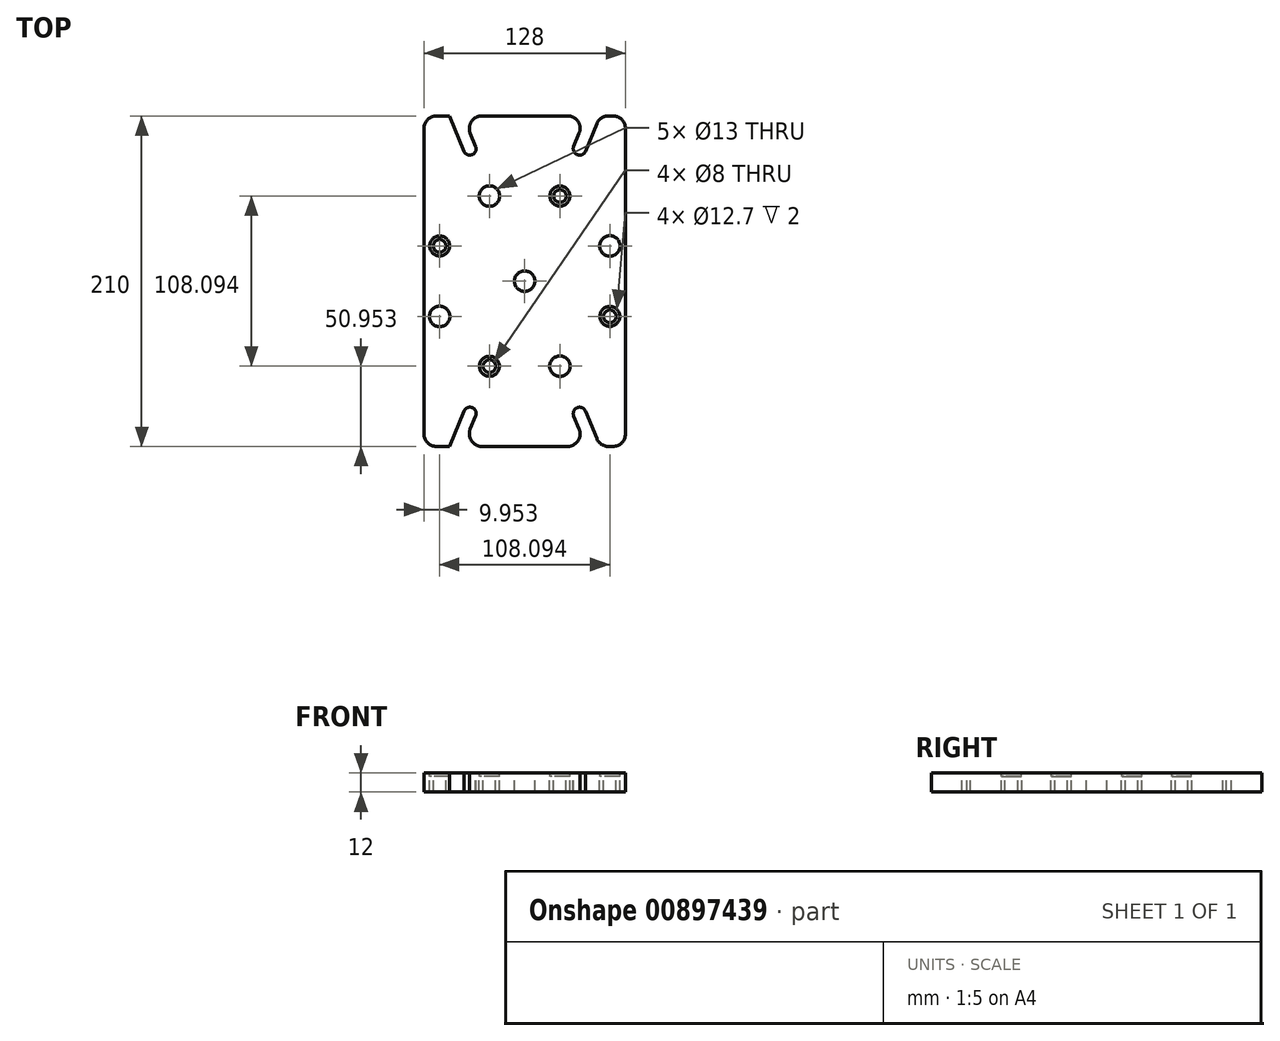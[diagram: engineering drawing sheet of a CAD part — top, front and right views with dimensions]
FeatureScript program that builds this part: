
annotation { "Feature Type Name" : "Feature", "Feature Type Description" : "" }
export const myFeature = defineFeature(function(context is Context, id is Id, definition is map)
    precondition{}
    {
        {
            var Q0;
            Q0=qCreatedBy(makeId("Top.planeOp"),FACE);
            var sketch = newSketch(context, id + "F0", { "sketchPlane" : qUnion([Q0])});
            skLineSegment(sketch, "E0.bottom", {"start": v(-64, 105) * mm, "end": v(64, 105) * mm});
            skLineSegment(sketch, "E0.top", {"start": v(-64, -105) * mm, "end": v(64, -105) * mm});
            skLineSegment(sketch, "E0.left", {"start": v(-64, 105) * mm, "end": v(-64, -105) * mm});
            skLineSegment(sketch, "E0.right", {"start": v(64, 105) * mm, "end": v(64, -105) * mm});
            skPoint(sketch, "E0.middle", {"position": v(0, 0) * mm});
            skSolve(sketch);
        }
        {
            var Q0;
            Q0=makeQuery(id+"F0.imprint","IMPRINT",FACE,{"disambiguationData":[TD([[makeQuery(id+"F0.imprint","IMPRINT",EDGE,{"derivedFrom":sQuery(id+"F0.wireOp",EDGE,"E0.bottom")}),-1.0]])]});
            extrude(context, id + "F1", {"entities" : qUnion([Q0]), "depth" : 12 * mm, "offsetDistance" : 25 * mm});
        }
        {
            var Q0;
            Q0=makeQuery(id+"F1.opExtrude","SWEPT_EDGE",EDGE,{"disambiguationData":[OSD([sQuery(id+"F0.wireOp",EDGE,"E0.top"),sQuery(id+"F0.wireOp",EDGE,"E0.left")])]});
            var Q1;
            Q1=makeQuery(id+"F1.opExtrude","SWEPT_EDGE",EDGE,{"disambiguationData":[OSD([sQuery(id+"F0.wireOp",EDGE,"E0.top"),sQuery(id+"F0.wireOp",EDGE,"E0.right")])]});
            var Q2;
            Q2=makeQuery(id+"F1.opExtrude","SWEPT_EDGE",EDGE,{"disambiguationData":[OSD([sQuery(id+"F0.wireOp",EDGE,"E0.bottom"),sQuery(id+"F0.wireOp",EDGE,"E0.right")])]});
            var Q3;
            Q3=makeQuery(id+"F1.opExtrude","SWEPT_EDGE",EDGE,{"disambiguationData":[OSD([sQuery(id+"F0.wireOp",EDGE,"E0.bottom"),sQuery(id+"F0.wireOp",EDGE,"E0.left")])]});
            fillet(context, id + "F2", {"entities" : qUnion([Q0, Q1, Q2, Q3]), "radius" : 8 * mm, "tangentPropagation" : true, "allowEdgeOverflow" : false});
        }
        {
            var Q0;
            Q0=makeQuery(id+"F1.opExtrude","CAP_FACE",FACE,{"disambiguationData":[OSD([sQuery(id+"F0.wireOp",EDGE,"E0.bottom"),sQuery(id+"F0.wireOp",EDGE,"E0.top"),sQuery(id+"F0.wireOp",EDGE,"E0.left"),sQuery(id+"F0.wireOp",EDGE,"E0.right")])],"isStart":false});
            var sketch = newSketch(context, id + "F3", { "sketchPlane" : qUnion([Q0])});
            skCircle(sketch, "E1", {"center": v(0, 0) * mm, "radius": 58.5 * mm, "construction": true});
            skLineSegment(sketch, "E2", {"start": v(77.06, 0) * mm, "end": v(-72.15, 0) * mm, "construction": true});
            skLineSegment(sketch, "E3", {"start": v(0, -115.81) * mm, "end": v(0, 119.74) * mm, "construction": true});
            skPoint(sketch, "E3.endSnap0", {"position": v(0, 105) * mm});
            skLineSegment(sketch, "E4", {"start": v(0, 0) * mm, "end": v(-83.82, 34.72) * mm, "construction": true});
            skCircle(sketch, "E5", {"center": v(-54.05, 22.39) * mm, "radius": 6.35 * mm});
            skCircle(sketch, "E6", {"center": v(-54.05, 22.39) * mm, "radius": 4 * mm});
            skLineSegment(sketch, "E7", {"start": v(0, 0) * mm, "end": v(59.7, -24.73) * mm, "construction": true});
            skLineSegment(sketch, "E8", {"start": v(0, 0) * mm, "end": v(59.72, 24.74) * mm, "construction": true});
            skLineSegment(sketch, "E9", {"start": v(47.91, -47.91) * mm, "end": v(0, 0) * mm, "construction": true});
            skLineSegment(sketch, "E10", {"start": v(0, 0) * mm, "end": v(-47.85, -47.85) * mm, "construction": true});
            skLineSegment(sketch, "E11", {"start": v(-47.85, -47.85) * mm, "end": v(0, 0) * mm, "construction": true});
            skLineSegment(sketch, "E12", {"start": v(0, 0) * mm, "end": v(-49.76, 49.76) * mm, "construction": true});
            skLineSegment(sketch, "E13", {"start": v(0, 0) * mm, "end": v(48.36, 48.36) * mm, "construction": true});
            skLineSegment(sketch, "E14", {"start": v(0, 0) * mm, "end": v(52.16, -125.92) * mm, "construction": true});
            skLineSegment(sketch, "E15", {"start": v(0, 0) * mm, "end": v(-48.89, -118.03) * mm, "construction": true});
            skLineSegment(sketch, "E16", {"start": v(0, 0) * mm, "end": v(-60.76, -25.17) * mm, "construction": true});
            skLineSegment(sketch, "E17", {"start": v(0, 0) * mm, "end": v(-48.6, 117.35) * mm, "construction": true});
            skLineSegment(sketch, "E18", {"start": v(0, 0) * mm, "end": v(49.9, 120.5) * mm, "construction": true});
            skCircle(sketch, "E19", {"center": v(54.05, -22.39) * mm, "radius": 4 * mm});
            skCircle(sketch, "E20", {"center": v(54.05, -22.39) * mm, "radius": 6.35 * mm});
            skCircle(sketch, "E21", {"center": v(-22.39, -54.05) * mm, "radius": 6.35 * mm});
            skCircle(sketch, "E22", {"center": v(-22.39, -54.05) * mm, "radius": 4 * mm});
            skCircle(sketch, "E23", {"center": v(22.39, 54.05) * mm, "radius": 6.35 * mm});
            skCircle(sketch, "E24", {"center": v(22.39, 54.05) * mm, "radius": 4 * mm});
            skCircle(sketch, "E25", {"center": v(-22.39, 54.05) * mm, "radius": 6.5 * mm});
            skCircle(sketch, "E26", {"center": v(-54.05, -22.39) * mm, "radius": 6.5 * mm});
            skCircle(sketch, "E27", {"center": v(22.39, -54.05) * mm, "radius": 6.5 * mm});
            skCircle(sketch, "E28", {"center": v(54.05, 22.39) * mm, "radius": 6.5 * mm});
            skSolve(sketch);
        }
        {
            var Q0;
            Q0=makeQuery(id+"F3.imprint","IMPRINT",FACE,{"disambiguationData":[TD([[makeQuery(id+"F3.imprint","IMPRINT",EDGE,{"derivedFrom":sQuery(id+"F3.wireOp",EDGE,"E25")}),1.0]])]});
            var Q1;
            Q1=makeQuery(id+"F3.imprint","IMPRINT",FACE,{"disambiguationData":[TD([[makeQuery(id+"F3.imprint","IMPRINT",EDGE,{"derivedFrom":sQuery(id+"F3.wireOp",EDGE,"E6")}),1.0]])]});
            var Q2;
            Q2=makeQuery(id+"F3.imprint","IMPRINT",FACE,{"disambiguationData":[TD([[makeQuery(id+"F3.imprint","IMPRINT",EDGE,{"derivedFrom":sQuery(id+"F3.wireOp",EDGE,"E26")}),1.0]])]});
            var Q3;
            Q3=makeQuery(id+"F3.imprint","IMPRINT",FACE,{"disambiguationData":[TD([[makeQuery(id+"F3.imprint","IMPRINT",EDGE,{"derivedFrom":sQuery(id+"F3.wireOp",EDGE,"E22")}),1.0]])]});
            var Q4;
            Q4=makeQuery(id+"F3.imprint","IMPRINT",FACE,{"disambiguationData":[TD([[makeQuery(id+"F3.imprint","IMPRINT",EDGE,{"derivedFrom":sQuery(id+"F3.wireOp",EDGE,"E27")}),1.0]])]});
            var Q5;
            Q5=makeQuery(id+"F3.imprint","IMPRINT",FACE,{"disambiguationData":[TD([[makeQuery(id+"F3.imprint","IMPRINT",EDGE,{"derivedFrom":sQuery(id+"F3.wireOp",EDGE,"E19")}),1.0]])]});
            var Q6;
            Q6=makeQuery(id+"F3.imprint","IMPRINT",FACE,{"disambiguationData":[TD([[makeQuery(id+"F3.imprint","IMPRINT",EDGE,{"derivedFrom":sQuery(id+"F3.wireOp",EDGE,"E28")}),1.0]])]});
            var Q7;
            Q7=makeQuery(id+"F3.imprint","IMPRINT",FACE,{"disambiguationData":[TD([[makeQuery(id+"F3.imprint","IMPRINT",EDGE,{"derivedFrom":sQuery(id+"F3.wireOp",EDGE,"E24")}),1.0]])]});
            extrude(context, id + "F4", {"entities" : qUnion([Q0, Q1, Q2, Q3, Q4, Q5, Q6, Q7]), "operationType" : NewBodyOperationType.REMOVE, "oppositeDirection" : true, "depth" : 25 * mm, "offsetDistance" : 25 * mm});
        }
        {
            var Q0;
            Q0=makeQuery(id+"F3.imprint","IMPRINT",FACE,{"disambiguationData":[TD([[makeQuery(id+"F3.imprint","IMPRINT",EDGE,{"derivedFrom":sQuery(id+"F3.wireOp",EDGE,"E5")}),1.0]])]});
            var Q1;
            Q1=makeQuery(id+"F3.imprint","IMPRINT",FACE,{"disambiguationData":[TD([[makeQuery(id+"F3.imprint","IMPRINT",EDGE,{"derivedFrom":sQuery(id+"F3.wireOp",EDGE,"E21")}),1.0]])]});
            var Q2;
            Q2=makeQuery(id+"F3.imprint","IMPRINT",FACE,{"disambiguationData":[TD([[makeQuery(id+"F3.imprint","IMPRINT",EDGE,{"derivedFrom":sQuery(id+"F3.wireOp",EDGE,"E19")}),-1.0]])]});
            var Q3;
            Q3=makeQuery(id+"F3.imprint","IMPRINT",FACE,{"disambiguationData":[TD([[makeQuery(id+"F3.imprint","IMPRINT",EDGE,{"derivedFrom":sQuery(id+"F3.wireOp",EDGE,"E23")}),1.0]])]});
            extrude(context, id + "F5", {"entities" : qUnion([Q0, Q1, Q2, Q3]), "operationType" : NewBodyOperationType.REMOVE, "oppositeDirection" : true, "depth" : 2 * mm, "offsetDistance" : 25 * mm});
        }
        {
            var Q0;
            Q0=makeQuery(id+"F3.imprint","IMPRINT",FACE,{"disambiguationData":[TD([[makeQuery(id+"F3.imprint","IMPRINT",EDGE,{"derivedFrom":sQuery(id+"F3.wireOp",EDGE,"E5")}),-1.0]])]});
            var sketch = newSketch(context, id + "F6", { "sketchPlane" : qUnion([Q0])});
            skCircle(sketch, "E29", {"center": v(0, 0) * mm, "radius": 91 * mm, "construction": true});
            skLineSegment(sketch, "E30", {"start": v(0, 0) * mm, "end": v(-54.7, 132.08) * mm, "construction": true});
            skLineSegment(sketch, "E31", {"start": v(0, 0) * mm, "end": v(-105.92, 0) * mm, "construction": true});
            skLineSegment(sketch, "E32", {"start": v(0, 0) * mm, "end": v(-51.64, -124.67) * mm, "construction": true});
            skLineSegment(sketch, "E33", {"start": v(0, 0) * mm, "end": v(47.52, -114.72) * mm, "construction": true});
            skLineSegment(sketch, "E34", {"start": v(0, 0) * mm, "end": v(51.4, 124.11) * mm, "construction": true});
            skArc(sketch, "E35", {"start": v(-38.55, 82.62) * mm, "mid": v(-33.3, 80.38) * mm, "end": v(-31.16, 85.68) * mm});
            skArc(sketch, "E36", {"start": v(31.16, 85.68) * mm, "mid": v(33.3, 80.38) * mm, "end": v(38.55, 82.62) * mm});
            skLineSegment(sketch, "E37", {"start": v(-38.49, 82.46) * mm, "end": v(-48.1, 105.67) * mm});
            skLineSegment(sketch, "E38", {"start": v(-31.1, 85.52) * mm, "end": v(-39.44, 105.67) * mm});
            skLineSegment(sketch, "E39", {"start": v(-48.1, 105.67) * mm, "end": v(-39.44, 105.67) * mm});
            skPoint(sketch, "E40.orphan", {"position": v(-39.16, 104.99) * mm});
            skPoint(sketch, "E41.orphan", {"position": v(-39.16, 105.67) * mm});
            skLineSegment(sketch, "E42.MirrorCS", {"start": v(38.49, 82.46) * mm, "end": v(48.1, 105.67) * mm});
            skArc(sketch, "E43.MirrorCS", {"start": v(38.55, 82.62) * mm, "mid": v(33.3, 80.38) * mm, "end": v(31.16, 85.68) * mm});
            skArc(sketch, "E44.MirrorCS", {"start": v(38.55, 82.62) * mm, "mid": v(38.52, 82.54) * mm, "end": v(38.49, 82.46) * mm});
            skLineSegment(sketch, "E45.MirrorCS", {"start": v(31.1, 85.52) * mm, "end": v(39.44, 105.67) * mm});
            skLineSegment(sketch, "E46.MirrorCS", {"start": v(48.1, 105.67) * mm, "end": v(39.44, 105.67) * mm});
            skLineSegment(sketch, "E47.MirrorCS", {"start": v(-38.49, -82.46) * mm, "end": v(-48.1, -105.67) * mm});
            skArc(sketch, "E48.MirrorCS", {"start": v(-38.55, -82.62) * mm, "mid": v(-33.3, -80.38) * mm, "end": v(-31.16, -85.68) * mm});
            skLineSegment(sketch, "E49.MirrorCS", {"start": v(-31.1, -85.52) * mm, "end": v(-39.44, -105.67) * mm});
            skLineSegment(sketch, "E50.MirrorCS", {"start": v(-48.1, -105.67) * mm, "end": v(-39.44, -105.67) * mm});
            skLineSegment(sketch, "E51.MirrorCS", {"start": v(38.49, -82.46) * mm, "end": v(48.1, -105.67) * mm});
            skArc(sketch, "E52.MirrorCS", {"start": v(38.55, -82.62) * mm, "mid": v(33.3, -80.38) * mm, "end": v(31.16, -85.68) * mm});
            skLineSegment(sketch, "E53.MirrorCS", {"start": v(31.1, -85.52) * mm, "end": v(39.44, -105.67) * mm});
            skLineSegment(sketch, "E54.MirrorCS", {"start": v(48.1, -105.67) * mm, "end": v(39.44, -105.67) * mm});
            skArc(sketch, "E55.trimOffspring", {"start": v(31.1, 85.52) * mm, "mid": v(31.13, 85.6) * mm, "end": v(31.16, 85.68) * mm});
            skSolve(sketch);
        }
        {
            var Q0;
            {var subQ0=sQuery(id+"F6.wireOp",EDGE,"E38");var subQ1=sQuery(id+"F6.wireOp",EDGE,"E35");var subQ9=makeQuery(id+"F6.imprint","INTERSECT",VERTEX,{"disambiguationData":[OD(0.0)],"derivedFrom":[subQ1,subQ0]});Q0=makeQuery(id+"F6.imprint","IMPRINT",FACE,{"disambiguationData":[TD([[makeQuery(id+"F6.imprint","IMPRINT",EDGE,{"disambiguationData":[TD([[subQ9,1.0]])],"derivedFrom":subQ1}),1.0]])]});}
            var Q1;
            {var subQ1=sQuery(id+"F6.wireOp",EDGE,"E48.MirrorCS");var subQ5=sQuery(id+"F6.wireOp",EDGE,"E47.MirrorCS");var subQ6=makeQuery(id+"F6.imprint","INTERSECT",VERTEX,{"disambiguationData":[OD(0.0)],"derivedFrom":[subQ5,subQ1]});Q1=makeQuery(id+"F6.imprint","IMPRINT",FACE,{"disambiguationData":[TD([[makeQuery(id+"F6.imprint","IMPRINT",EDGE,{"disambiguationData":[TD([[subQ6,-1.0]])],"derivedFrom":subQ5}),1.0]])]});}
            var Q2;
            {var subQ0=sQuery(id+"F6.wireOp",EDGE,"E52.MirrorCS");var subQ1=sQuery(id+"F6.wireOp",EDGE,"E51.MirrorCS");var subQ8=makeQuery(id+"F6.imprint","INTERSECT",VERTEX,{"disambiguationData":[OD(0.0)],"derivedFrom":[subQ1,subQ0]});Q2=makeQuery(id+"F6.imprint","IMPRINT",FACE,{"disambiguationData":[TD([[makeQuery(id+"F6.imprint","IMPRINT",EDGE,{"disambiguationData":[TD([[subQ8,-1.0]])],"derivedFrom":subQ1}),-1.0]])]});}
            var Q3;
            {var subQ0=sQuery(id+"F6.wireOp",EDGE,"E45.MirrorCS");var subQ1=sQuery(id+"F6.wireOp",EDGE,"E36");var subQ9=makeQuery(id+"F6.imprint","INTERSECT",VERTEX,{"disambiguationData":[OD(1.0)],"derivedFrom":[subQ1,subQ0]});Q3=makeQuery(id+"F6.imprint","IMPRINT",FACE,{"disambiguationData":[TD([[makeQuery(id+"F6.imprint","IMPRINT",EDGE,{"disambiguationData":[TD([[subQ9,-1.0]])],"derivedFrom":subQ1}),1.0]])]});}
            extrude(context, id + "F7", {"entities" : qUnion([Q0, Q1, Q2, Q3]), "operationType" : NewBodyOperationType.REMOVE, "oppositeDirection" : true, "depth" : 25 * mm, "offsetDistance" : 25 * mm});
        }
        {
            var Q0;
            Q0=makeQuery(id+"F7.boolean.opBoolean","COPY",EDGE,{"derivedFrom":makeQuery(id+"F7.opExtrude","SWEPT_EDGE",EDGE,{"disambiguationData":[OSD([sQuery(id+"F0.wireOp",EDGE,"E0.bottom"),sQuery(id+"F6.wireOp",EDGE,"E37")])]})});
            var Q1;
            Q1=makeQuery(id+"F7.boolean.opBoolean","COPY",EDGE,{"derivedFrom":makeQuery(id+"F7.opExtrude","SWEPT_EDGE",EDGE,{"disambiguationData":[OSD([sQuery(id+"F0.wireOp",EDGE,"E0.bottom"),sQuery(id+"F6.wireOp",EDGE,"E38")])]})});
            var Q2;
            Q2=makeQuery(id+"F7.boolean.opBoolean","COPY",EDGE,{"derivedFrom":makeQuery(id+"F7.opExtrude","SWEPT_EDGE",EDGE,{"disambiguationData":[OSD([sQuery(id+"F0.wireOp",EDGE,"E0.bottom"),sQuery(id+"F6.wireOp",EDGE,"E45.MirrorCS")])]})});
            var Q3;
            Q3=makeQuery(id+"F7.boolean.opBoolean","COPY",EDGE,{"derivedFrom":makeQuery(id+"F7.opExtrude","SWEPT_EDGE",EDGE,{"disambiguationData":[OSD([sQuery(id+"F0.wireOp",EDGE,"E0.bottom"),sQuery(id+"F6.wireOp",EDGE,"E42.MirrorCS")])]})});
            var Q4;
            Q4=makeQuery(id+"F7.boolean.opBoolean","COPY",EDGE,{"derivedFrom":makeQuery(id+"F7.opExtrude","SWEPT_EDGE",EDGE,{"disambiguationData":[OSD([sQuery(id+"F0.wireOp",EDGE,"E0.top"),sQuery(id+"F6.wireOp",EDGE,"E51.MirrorCS")])]})});
            var Q5;
            Q5=makeQuery(id+"F7.boolean.opBoolean","COPY",EDGE,{"derivedFrom":makeQuery(id+"F7.opExtrude","SWEPT_EDGE",EDGE,{"disambiguationData":[OSD([sQuery(id+"F0.wireOp",EDGE,"E0.top"),sQuery(id+"F6.wireOp",EDGE,"E53.MirrorCS")])]})});
            var Q6;
            Q6=makeQuery(id+"F7.boolean.opBoolean","COPY",EDGE,{"derivedFrom":makeQuery(id+"F7.opExtrude","SWEPT_EDGE",EDGE,{"disambiguationData":[OSD([sQuery(id+"F0.wireOp",EDGE,"E0.top"),sQuery(id+"F6.wireOp",EDGE,"E49.MirrorCS")])]})});
            var Q7;
            Q7=makeQuery(id+"F7.boolean.opBoolean","COPY",EDGE,{"derivedFrom":makeQuery(id+"F7.opExtrude","SWEPT_EDGE",EDGE,{"disambiguationData":[OSD([sQuery(id+"F0.wireOp",EDGE,"E0.top"),sQuery(id+"F6.wireOp",EDGE,"E47.MirrorCS")])]})});
            fillet(context, id + "F8", {"entities" : qUnion([Q0, Q1, Q2, Q3, Q4, Q5, Q6, Q7]), "radius" : 8 * mm, "tangentPropagation" : true, "allowEdgeOverflow" : false});
        }
        {
            var Q0;
            Q0=makeQuery(id+"F1.opExtrude","CAP_FACE",FACE,{"disambiguationData":[OSD([sQuery(id+"F0.wireOp",EDGE,"E0.bottom"),sQuery(id+"F0.wireOp",EDGE,"E0.top"),sQuery(id+"F0.wireOp",EDGE,"E0.left"),sQuery(id+"F0.wireOp",EDGE,"E0.right")])],"isStart":false});
            var sketch = newSketch(context, id + "F9", { "sketchPlane" : qUnion([Q0])});
            skSolve(sketch);
        }
        {
            var Q0;
            {var subQ1=sQuery(id+"F0.wireOp",EDGE,"E0.left");Q0=makeQuery(id+"F9.imprint","IMPRINT",FACE,{"disambiguationData":[TD([[makeQuery(id+"F9.imprint","IMPRINT",EDGE,{"derivedFrom":makeQuery(id+"F1.opExtrude","CAP_EDGE",EDGE,{"disambiguationData":[OSD([subQ1])],"isStart":false})}),1.0]])]});}
            var sketch = newSketch(context, id + "F10", { "sketchPlane" : qUnion([Q0])});
            skCircle(sketch, "E56", {"center": v(0, 0) * mm, "radius": 6.5 * mm});
            skSolve(sketch);
        }
        {
            var Q0;
            Q0 = qSketchRegion(id + "F10", true);
            extrude(context, id + "F11", {"entities" : qUnion([Q0]), "operationType" : NewBodyOperationType.REMOVE, "oppositeDirection" : true, "depth" : 25 * mm, "offsetDistance" : 25 * mm});
        }
    });
